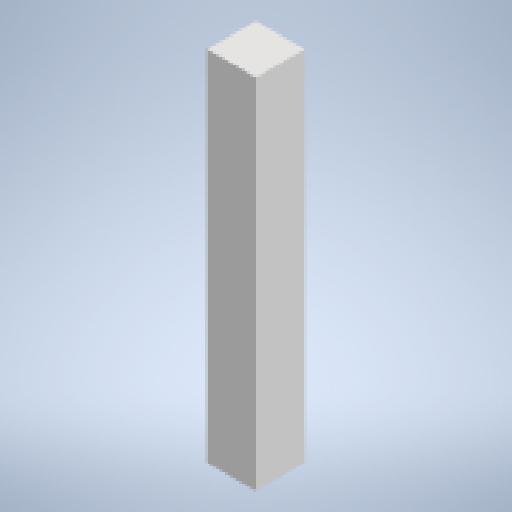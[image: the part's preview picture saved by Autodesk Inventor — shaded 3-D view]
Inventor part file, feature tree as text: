
AUTODESK INVENTOR PART (.ipt)
format: ipt  version: 2024 (Build 280153000, 153)  size: 133,632 bytes
history: native  units: mm
features: extrude x1, sketch x1
ambient origin geometry x8: Origin, YZ Plane, XZ Plane, XY Plane, X Axis, Y Axis, Z Axis, Center Point
bodies: Solid1 (feature_tree)
feature tree (2):
  extrude  "Extrusion1"  Depth=45.0mm
  sketch  "Sketch1"  dims[d0=45.0mm d1=45.0mm d2=330.0mm d3=0.0mm]
